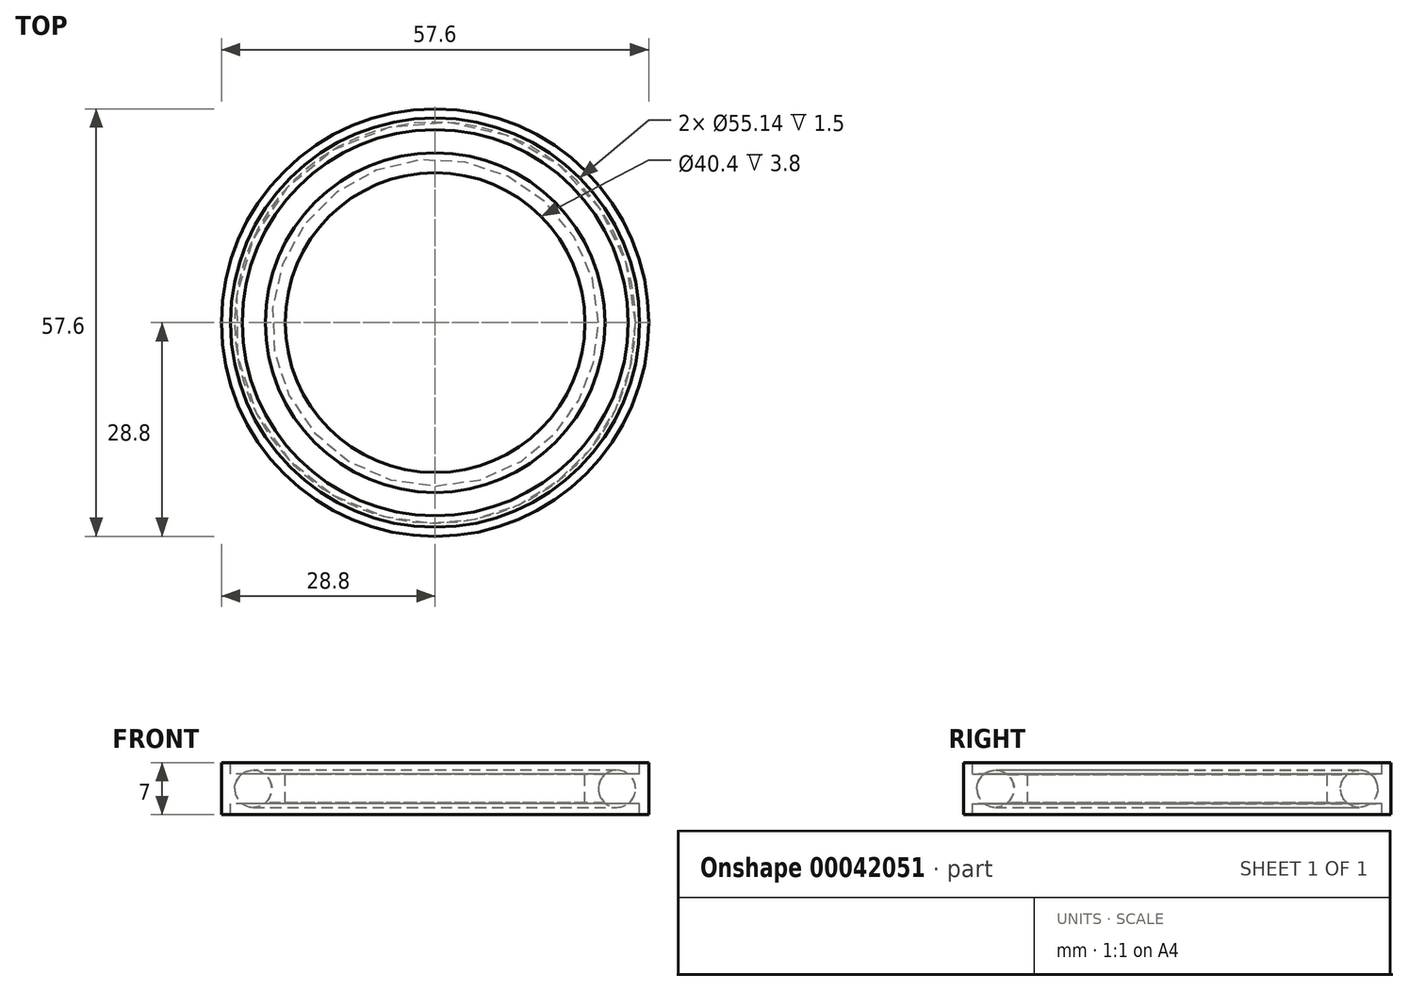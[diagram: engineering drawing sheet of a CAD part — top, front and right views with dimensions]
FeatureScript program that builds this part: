
annotation { "Feature Type Name" : "Feature", "Feature Type Description" : "" }
export const myFeature = defineFeature(function(context is Context, id is Id, definition is map)
    precondition{}
    {
        {
            var Q0;
            Q0=qCreatedBy(makeId("Front.planeOp"),FACE);
            var sketch = newSketch(context, id + "F0", { "sketchPlane" : qUnion([Q0])});
            skLineSegment(sketch, "E0", {"start": v(0, 7) * mm, "end": v(0, 0) * mm, "construction": true});
            skLineSegment(sketch, "E1", {"start": v(28.8, 7) * mm, "end": v(28.8, 0) * mm});
            skLineSegment(sketch, "E2", {"start": v(28.8, 7) * mm, "end": v(27.57, 7) * mm});
            skLineSegment(sketch, "E3", {"start": v(27.57, 7) * mm, "end": v(27.57, 5.5) * mm});
            skLineSegment(sketch, "E4", {"start": v(27.57, 5.5) * mm, "end": v(26.01, 5.5) * mm});
            skLineSegment(sketch, "E5", {"start": v(26.01, 1.5) * mm, "end": v(27.57, 1.5) * mm});
            skLineSegment(sketch, "E6", {"start": v(27.57, 1.5) * mm, "end": v(27.57, 0) * mm});
            skLineSegment(sketch, "E7", {"start": v(27.57, 0) * mm, "end": v(28.8, 0) * mm});
            skArc(sketch, "E8", {"start": v(26.01, 1.5) * mm, "mid": v(27.01, 3.5) * mm, "end": v(26.01, 5.5) * mm});
            skCircle(sketch, "E9", {"center": v(24.51, 3.5) * mm, "radius": 2.5 * mm});
            skLineSegment(sketch, "E10", {"start": v(24.51, 3.5) * mm, "end": v(18.55, 3.5) * mm, "construction": true});
            skLineSegment(sketch, "E11", {"start": v(22.89, 5.4) * mm, "end": v(20.2, 5.4) * mm});
            skLineSegment(sketch, "E12", {"start": v(20.2, 5.4) * mm, "end": v(20.2, 1.6) * mm});
            skLineSegment(sketch, "E13", {"start": v(20.2, 1.6) * mm, "end": v(22.89, 1.6) * mm});
            skSolve(sketch);
        }
        {
            var Q0;
            Q0=makeQuery(id+"F0.imprint","IMPRINT",FACE,{"disambiguationData":[TD([[makeQuery(id+"F0.imprint","IMPRINT",EDGE,{"derivedFrom":sQuery(id+"F0.wireOp",EDGE,"E1")}),-1.0]])]});
            var Q1;
            Q1=sQuery(id+"F0.wireOp",EDGE,"E0");
            revolve(context, id + "F1", {"entities" : qUnion([Q0]), "axis" : qUnion([Q1]), "revolveType" : RevolveType.FULL});
        }
        {
            var Q0;
            {var subQ1=sQuery(id+"F0.wireOp",EDGE,"E11");Q0=makeQuery(id+"F0.imprint","IMPRINT",FACE,{"disambiguationData":[TD([[makeQuery(id+"F0.imprint","IMPRINT",EDGE,{"derivedFrom":subQ1}),1.0]])]});}
            var Q1;
            Q1=sQuery(id+"F0.wireOp",EDGE,"E0");
            revolve(context, id + "F2", {"entities" : qUnion([Q0]), "axis" : qUnion([Q1]), "revolveType" : RevolveType.FULL});
        }
        {
            var Q0;
            {var subQ0=sQuery(id+"F0.wireOp",EDGE,"E9");var subQ2=makeQuery(id+"F0.imprint","INTERSECT",VERTEX,{"derivedFrom":[sQuery(id+"F0.wireOp",EDGE,"E4"),subQ0]});Q0=makeQuery(id+"F0.imprint","IMPRINT",FACE,{"disambiguationData":[TD([[makeQuery(id+"F0.imprint","IMPRINT",EDGE,{"disambiguationData":[TD([[subQ2,-1.0]])],"derivedFrom":subQ0}),1.0]])]});}
            var Q1;
            Q1=sQuery(id+"F0.wireOp",EDGE,"E0");
            revolve(context, id + "F3", {"entities" : qUnion([Q0]), "axis" : qUnion([Q1]), "revolveType" : RevolveType.FULL});
        }
    });
